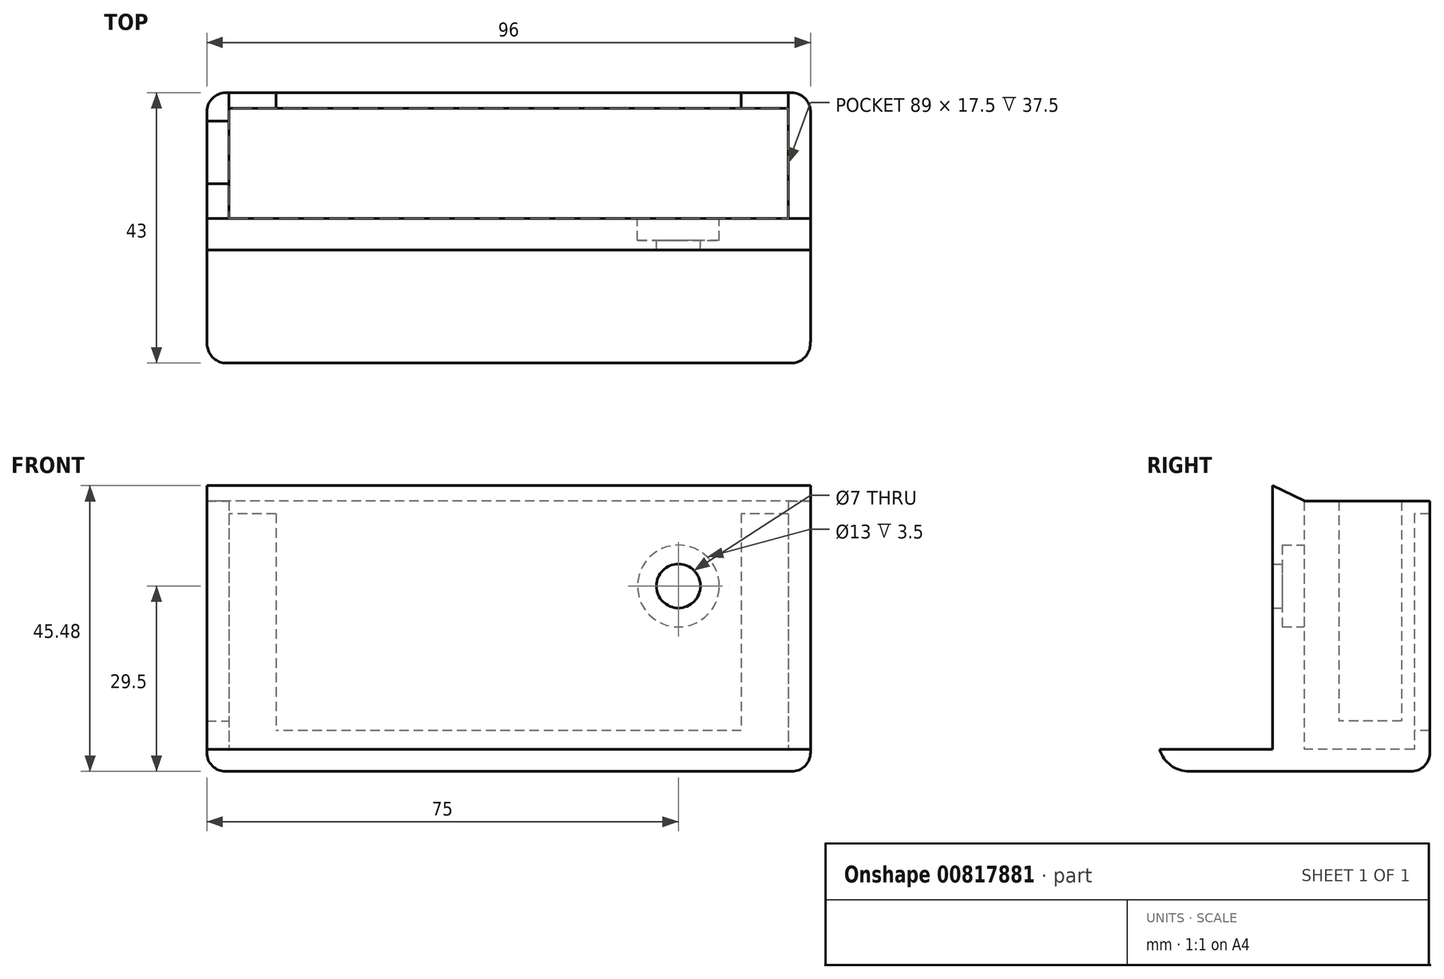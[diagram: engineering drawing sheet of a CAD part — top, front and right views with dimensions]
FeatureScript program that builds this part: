
annotation { "Feature Type Name" : "Feature", "Feature Type Description" : "" }
export const myFeature = defineFeature(function(context is Context, id is Id, definition is map)
    precondition{}
    {
        {
            var Q0;
            Q0=qCreatedBy(makeId("Top.planeOp"),FACE);
            var sketch = newSketch(context, id + "F0", { "sketchPlane" : qUnion([Q0])});
            skLineSegment(sketch, "E0.bottom", {"start": v(48, 21.5) * mm, "end": v(-48, 21.5) * mm});
            skLineSegment(sketch, "E0.top", {"start": v(48, -21.5) * mm, "end": v(-48, -21.5) * mm});
            skLineSegment(sketch, "E0.left", {"start": v(48, 21.5) * mm, "end": v(48, -21.5) * mm});
            skLineSegment(sketch, "E0.right", {"start": v(-48, 21.5) * mm, "end": v(-48, -21.5) * mm});
            skPoint(sketch, "E0.middle", {"position": v(0, 0) * mm});
            skSolve(sketch);
        }
        {
            var Q0;
            Q0 = qSketchRegion(id + "F0", true);
            extrude(context, id + "F1", {"entities" : qUnion([Q0]), "depth" : 3.5 * mm, "offsetDistance" : 25 * mm});
        }
        {
            var Q0;
            Q0=makeQuery(id+"F1.opExtrude","CAP_EDGE",EDGE,{"disambiguationData":[OSD([sQuery(id+"F0.wireOp",EDGE,"E0.top")])],"isStart":true});
            fillet(context, id + "F2", {"entities" : qUnion([Q0]), "radius" : 5 * mm, "tangentPropagation" : true, "allowEdgeOverflow" : false});
        }
        {
            var Q0;
            Q0=makeQuery(id+"F1.opExtrude","CAP_FACE",FACE,{"disambiguationData":[OSD([sQuery(id+"F0.wireOp",EDGE,"E0.bottom"),sQuery(id+"F0.wireOp",EDGE,"E0.top"),sQuery(id+"F0.wireOp",EDGE,"E0.left"),sQuery(id+"F0.wireOp",EDGE,"E0.right")])],"isStart":false});
            var sketch = newSketch(context, id + "F3", { "sketchPlane" : qUnion([Q0])});
            skLineSegment(sketch, "E1.bottom", {"start": v(-48, -3.5) * mm, "end": v(48, -3.5) * mm});
            skLineSegment(sketch, "E1.top", {"start": v(-48, 1.5) * mm, "end": v(48, 1.5) * mm});
            skLineSegment(sketch, "E1.left", {"start": v(-48, -3.5) * mm, "end": v(-48, 1.5) * mm});
            skLineSegment(sketch, "E1.right", {"start": v(48, -3.5) * mm, "end": v(48, 1.5) * mm});
            skLineSegment(sketch, "E2.bottom", {"start": v(48, 21.5) * mm, "end": v(44.5, 21.5) * mm});
            skLineSegment(sketch, "E2.top", {"start": v(48, 1.5) * mm, "end": v(44.5, 1.5) * mm});
            skLineSegment(sketch, "E2.left", {"start": v(48, 21.5) * mm, "end": v(48, 1.5) * mm});
            skLineSegment(sketch, "E2.right", {"start": v(44.5, 21.5) * mm, "end": v(44.5, 1.5) * mm});
            skLineSegment(sketch, "E3.MirrorCS", {"start": v(-44.5, 21.5) * mm, "end": v(-44.5, 1.5) * mm});
            skLineSegment(sketch, "E4.MirrorCS", {"start": v(-48, 1.5) * mm, "end": v(-44.5, 1.5) * mm});
            skLineSegment(sketch, "E5.MirrorCS", {"start": v(-48, 21.5) * mm, "end": v(-48, 1.5) * mm});
            skLineSegment(sketch, "E6.MirrorCS", {"start": v(-48, 21.5) * mm, "end": v(-44.5, 21.5) * mm});
            skLineSegment(sketch, "E7.bottom", {"start": v(44.5, 21.5) * mm, "end": v(-44.5, 21.5) * mm});
            skLineSegment(sketch, "E7.top", {"start": v(44.5, 19) * mm, "end": v(-44.5, 19) * mm});
            skLineSegment(sketch, "E7.left", {"start": v(44.5, 21.5) * mm, "end": v(44.5, 19) * mm});
            skLineSegment(sketch, "E7.right", {"start": v(-44.5, 21.5) * mm, "end": v(-44.5, 19) * mm});
            skSolve(sketch);
        }
        {
            var Q0;
            Q0=makeQuery(id+"F3.imprint","IMPRINT",FACE,{"disambiguationData":[TD([[makeQuery(id+"F3.imprint","IMPRINT",EDGE,{"derivedFrom":sQuery(id+"F3.wireOp",EDGE,"E1.bottom")}),1.0]])]});
            extrude(context, id + "F4", {"entities" : qUnion([Q0]), "operationType" : NewBodyOperationType.ADD, "depth" : 42 * mm, "offsetDistance" : 25 * mm});
        }
        {
            var Q0;
            Q0=makeQuery(id+"F4.opExtrude","CAP_EDGE",EDGE,{"disambiguationData":[OSD([sQuery(id+"F3.wireOp",EDGE,"E1.top")])],"isStart":false});
            chamfer(context, id + "F5", {"entities" : qUnion([Q0]), "chamferType" : ChamferType.OFFSET_ANGLE, "width" : 2.4 * mm, "oppositeDirection" : false, "angle" : 64.5 * degree, "tangentPropagation" : true});
        }
        {
            var Q0;
            Q0=makeQuery(id+"F4.opExtrude","SWEPT_FACE",FACE,{"disambiguationData":[OSD([sQuery(id+"F3.wireOp",EDGE,"E1.top")])]});
            var sketch = newSketch(context, id + "F6", { "sketchPlane" : qUnion([Q0])});
            skCircle(sketch, "E8", {"center": v(-27, 29.5) * mm, "radius": 4.14 * mm});
            skSolve(sketch);
        }
        {
            var Q0;
            Q0=sQuery(id+"F6.wireOp",VERTEX,"E8.center");
            var Q1;
            Q1=makeQuery(id+"F1.opExtrude","SWEPT_BODY",BODY,{"disambiguationData":[OSD([sQuery(id+"F0.wireOp",EDGE,"E0.bottom"),sQuery(id+"F0.wireOp",EDGE,"E0.top"),sQuery(id+"F0.wireOp",EDGE,"E0.left"),sQuery(id+"F0.wireOp",EDGE,"E0.right")])]});
            hole(context, id + "F7", {"style" : HoleStyle.C_BORE, "endStyle" : HoleEndStyle.THROUGH, "holeDiameter" : 7 * mm, "cBoreDiameter" : 13 * mm, "cBoreDepth" : 3.5 * mm, "majorDiameter" : 5 * mm, "isTappedThrough" : true, "tappedDepth" : 12 * mm, "tapClearance" : 3, "locations" : qUnion([Q0]), "scope" : qUnion([Q1])});
        }
        {
            var Q0;
            Q0=makeQuery(id+"F3.imprint","IMPRINT",FACE,{"disambiguationData":[TD([[makeQuery(id+"F3.imprint","IMPRINT",EDGE,{"derivedFrom":sQuery(id+"F3.wireOp",EDGE,"E2.bottom")}),1.0]])]});
            var Q1;
            Q1=makeQuery(id+"F3.imprint","IMPRINT",FACE,{"disambiguationData":[TD([[makeQuery(id+"F3.imprint","IMPRINT",EDGE,{"derivedFrom":sQuery(id+"F3.wireOp",EDGE,"E3.MirrorCS")}),-1.0]])]});
            extrude(context, id + "F8", {"entities" : qUnion([Q0, Q1]), "operationType" : NewBodyOperationType.ADD, "depth" : 39.5 * mm, "offsetDistance" : 25 * mm});
        }
        {
            var Q0;
            Q0=makeQuery(id+"F3.imprint","IMPRINT",FACE,{"disambiguationData":[TD([[makeQuery(id+"F3.imprint","IMPRINT",EDGE,{"derivedFrom":sQuery(id+"F3.wireOp",EDGE,"E7.bottom")}),1.0]])]});
            extrude(context, id + "F9", {"entities" : qUnion([Q0]), "operationType" : NewBodyOperationType.ADD, "depth" : 3 * mm, "offsetDistance" : 25 * mm});
        }
        {
            var Q0;
            Q0=makeQuery(id+"F9.opExtrude","CAP_FACE",FACE,{"disambiguationData":[OSD([sQuery(id+"F3.wireOp",EDGE,"E7.bottom"),sQuery(id+"F3.wireOp",EDGE,"E7.top"),sQuery(id+"F3.wireOp",EDGE,"E7.left"),sQuery(id+"F3.wireOp",EDGE,"E7.right")])],"isStart":false});
            var sketch = newSketch(context, id + "F10", { "sketchPlane" : qUnion([Q0])});
            skLineSegment(sketch, "E9.bottom", {"start": v(44.5, 21.5) * mm, "end": v(37, 21.5) * mm});
            skLineSegment(sketch, "E9.top", {"start": v(44.5, 19) * mm, "end": v(37, 19) * mm});
            skLineSegment(sketch, "E9.left", {"start": v(44.5, 21.5) * mm, "end": v(44.5, 19) * mm});
            skLineSegment(sketch, "E9.right", {"start": v(37, 21.5) * mm, "end": v(37, 19) * mm});
            skLineSegment(sketch, "E10.MirrorCS", {"start": v(-44.5, 19) * mm, "end": v(-37, 19) * mm});
            skLineSegment(sketch, "E11.MirrorCS", {"start": v(-37, 21.5) * mm, "end": v(-37, 19) * mm});
            skLineSegment(sketch, "E12.MirrorCS", {"start": v(-44.5, 21.5) * mm, "end": v(-37, 21.5) * mm});
            skLineSegment(sketch, "E13.MirrorCS", {"start": v(-44.5, 21.5) * mm, "end": v(-44.5, 19) * mm});
            skSolve(sketch);
        }
        {
            var Q0;
            Q0 = qSketchRegion(id + "F10", true);
            extrude(context, id + "F11", {"entities" : qUnion([Q0]), "operationType" : NewBodyOperationType.ADD, "depth" : 34.5 * mm, "offsetDistance" : 25 * mm});
        }
        {
            var Q0;
            Q0=makeQuery(id+"F8.opExtrude","SWEPT_FACE",FACE,{"disambiguationData":[OSD([sQuery(id+"F3.wireOp",EDGE,"E3.MirrorCS"),sQuery(id+"F3.wireOp",EDGE,"E7.right")])]});
            var sketch = newSketch(context, id + "F12", { "sketchPlane" : qUnion([Q0])});
            skLineSegment(sketch, "E14.bottom", {"start": v(17, 43) * mm, "end": v(7, 43) * mm});
            skLineSegment(sketch, "E14.top", {"start": v(17, 8) * mm, "end": v(7, 8) * mm});
            skLineSegment(sketch, "E14.left", {"start": v(17, 43) * mm, "end": v(17, 8) * mm});
            skLineSegment(sketch, "E14.right", {"start": v(7, 43) * mm, "end": v(7, 8) * mm});
            skPoint(sketch, "E15", {"position": v(12, 43) * mm});
            skSolve(sketch);
        }
        {
            var Q0;
            Q0=makeQuery(id+"F12.imprint","IMPRINT",FACE,{"disambiguationData":[TD([[makeQuery(id+"F12.imprint","IMPRINT",EDGE,{"derivedFrom":sQuery(id+"F12.wireOp",EDGE,"E14.bottom")}),1.0]])]});
            extrude(context, id + "F13", {"entities" : qUnion([Q0]), "operationType" : NewBodyOperationType.REMOVE, "oppositeDirection" : true, "depth" : 3.5 * mm, "offsetDistance" : 25 * mm});
        }
        {
            var Q0;
            Q0=makeQuery(id+"F8.boolean.opBoolean","MERGE",EDGE,{"derivedFrom":[makeQuery(id+"F1.opExtrude","SWEPT_EDGE",EDGE,{"disambiguationData":[OSD([sQuery(id+"F0.wireOp",EDGE,"E0.bottom"),sQuery(id+"F0.wireOp",EDGE,"E0.right")])]}),makeQuery(id+"F8.opExtrude","SWEPT_EDGE",EDGE,{"disambiguationData":[OSD([sQuery(id+"F3.wireOp",EDGE,"E5.MirrorCS"),sQuery(id+"F3.wireOp",EDGE,"E6.MirrorCS")])]})]});
            var Q1;
            Q1=makeQuery(id+"F8.boolean.opBoolean","MERGE",EDGE,{"derivedFrom":[makeQuery(id+"F1.opExtrude","SWEPT_EDGE",EDGE,{"disambiguationData":[OSD([sQuery(id+"F0.wireOp",EDGE,"E0.bottom"),sQuery(id+"F0.wireOp",EDGE,"E0.left")])]}),makeQuery(id+"F8.opExtrude","SWEPT_EDGE",EDGE,{"disambiguationData":[OSD([sQuery(id+"F3.wireOp",EDGE,"E2.bottom"),sQuery(id+"F3.wireOp",EDGE,"E2.left")])]})]});
            var Q2;
            Q2=makeQuery(id+"F2.opFillet","BLEND_EDGE",EDGE,{"blendedFrom":[makeQuery(id+"F1.opExtrude","CAP_EDGE",EDGE,{"disambiguationData":[OSD([sQuery(id+"F0.wireOp",EDGE,"E0.top")])],"isStart":true}),makeQuery(id+"F1.opExtrude","SWEPT_FACE",FACE,{"disambiguationData":[OSD([sQuery(id+"F0.wireOp",EDGE,"E0.right")])]})],"blendedInto":[makeQuery(id+"F1.opExtrude","SWEPT_FACE",FACE,{"disambiguationData":[OSD([sQuery(id+"F0.wireOp",EDGE,"E0.right")])]})]});
            var Q3;
            Q3=makeQuery(id+"F2.opFillet","BLEND_EDGE",EDGE,{"blendedFrom":[makeQuery(id+"F1.opExtrude","CAP_EDGE",EDGE,{"disambiguationData":[OSD([sQuery(id+"F0.wireOp",EDGE,"E0.top")])],"isStart":true}),makeQuery(id+"F1.opExtrude","SWEPT_FACE",FACE,{"disambiguationData":[OSD([sQuery(id+"F0.wireOp",EDGE,"E0.left")])]})],"blendedInto":[makeQuery(id+"F1.opExtrude","SWEPT_FACE",FACE,{"disambiguationData":[OSD([sQuery(id+"F0.wireOp",EDGE,"E0.left")])]})]});
            var Q4;
            Q4=makeQuery(id+"F1.opExtrude","CAP_EDGE",EDGE,{"disambiguationData":[OSD([sQuery(id+"F0.wireOp",EDGE,"E0.bottom")])],"isStart":true});
            fillet(context, id + "F14", {"entities" : qUnion([Q0, Q1, Q2, Q3, Q4]), "radius" : 3 * mm, "tangentPropagation" : true, "allowEdgeOverflow" : false});
        }
    });
